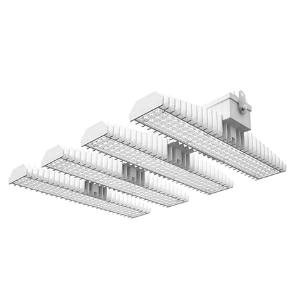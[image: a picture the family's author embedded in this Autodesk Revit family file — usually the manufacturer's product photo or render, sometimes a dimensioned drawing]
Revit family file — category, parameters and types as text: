
# Revit family: 3f_filippi_-_3f_lem_ht_ampio_3f_filippi_-_59028_a0811_-_3f_lem_4_ht_led_120_cr_ampio___vt_8aed
name_source: partatom
category: Lighting Fixtures
units: mm (PartAtom-declared; Revit-internal decimal feet)

## family parameters
Cut with Voids When Loaded = No
Host = Face
Light Source = No
Part Type = Normal
Room Calculation Point = No
Round Connector Dimension = Use Diameter
Shared = No

## types (1)
- 3F Filippi - 3F LEM HT Ampio (1 x LED, 20238 lm, 136 W, 4000 K)
    Apparent Load = 136 VA
    Approval mark = ENEC
    CIE Flux Codes = 60 92 99 100 100
    Color Rendering = 80
    Color Temperature = 4000 K
    Control Gear = Electronic ballast
    Default Elevation = 1800 mm
    Description = Industrial luminaire with high light output and high luminous efficiency designed with the most innovative technologies for environments with temperature up to 70°C.

ILLUMINOTECHNICAL
Luminous efficiency 100% (DLOR 99%, ULOR 1%).
Initial luminous flux of the luminaire 20238 lm.
Direct symmetric wide distribution: the illuminated area has a rectangular shape.
Installation Interdistance Transv.D = 1.58 x hu - Long.D = 1.45 x hu.
Tabular UGR (CIE 117 - 4H-8H; S=0.25H; 70/50/20): RUG 21.3 - 22.4.
Beam angle: 93° - 99°.
Luminous efficacy 149 lm/W.
Lifetime (L93/B10): 30000 h. (tq+25°C)
Lifetime (L90/B10): 50000 h. (tq+25°C)
Lifetime (L85/B10): 80000 h. (tq+25°C)
Lifetime (L80/B10): 100000 h. (tq+25°C)
Lifetime (L85/B10): 50000 h. (tq+70°C)
Sudden decreased luminous flux after 50000 hours: 0% (C0).
Photobiological safety in compliance with IEC/TR 62778: RG0 risk exempt, (IEC 62471).
In compliance with IEC/EN 62722-2-1 - IEC/EN 62717 standards.
Luminous flux at +70°C: -13.5%.

SOURCE
4 Mid-Power linear LED modules 30W/840.
Energy efficiency class (UE 2019/2020 - UE 2019/2015): C.
CIE 13.3 Colour rendering index: CRI >80 (R9 <50%).
IES TM-30 Fidelity Index: Rf = 84 Rg = 95.
CCT nominal colour temperature 4000 K.
Colour initial tolerance (MacAdam): SDCM 3.

MECHANICAL
Passive modular heatsinks in die-casted aluminium, painted in white colour.
To optimize the thermal management of the LED module, the heatsinks are oversized and provided with self-cleaning of cooling fins.
Wiring body in aluminium and galvanised steel anchored solidly to the sinks and thermally separated.
3F Lens lenses with high luminous efficiency, transparent polycarbonate, fixed to the LED modules.
Fixing brackets in stainless steel.
Luminaire with limited surface temperature. - D - (EN 60598-2-24)
Dimensions: 757x542 mm, height 133 mm. Weight 19.273 kg.
IP65 protection degree.
Mechanical strength to impacts IK08 (5 joule).
Glow-wire test resistance 850°C.

ELECTRICAL
Halogen Free electronic wiring 230V-50/60Hz, power factor 0.97, THD <25%, constant output current, class I, 2 driver.
Power of the luminaire 136 W.
CE - IEC 60598-1 - EN 60598-1.
SAFE FLICKER: PstLM=<1 and SVM=<0.4 (IEC TR 61547-1 and IEC TR 63158), to ensure a more comfortable and safe light.
Luminaire compliant with EN 60598-2-22 for power supply from a centralised emergency system CPSS (Central Power Supply System), not incorporated in the luminaire - high risk areas excluded. The default power and flux are 100% in AC and 100% in DC.
Ambient temperature from -30°C to +70°C.
Temperature class T6 max 85°C.
Quick connection via M20 3P connector with 9-13 mm tightening range.
Power unit positioned on a separate compartment by the LED module to ensure optimum temperatures of cabling components, to be inspectable and maintainable.
Relative humidity UR: <85%.

INSTALLATION
Ceiling / Suspended / Wall.
All accessories dedicated to this product are available on the Catalog and on our website www.3F-Filippi.com.

ACCESSORIES
A0811 - VT transparent glass, tempered, not flammable, with sealing gasket.
One required for each light module. The pack contains 10 pieces.

APPLICATIONS
In commercial environments, exhibition and industrial areas, stores, open areas.
Applications with high ambient temperature up to 70°C.

WARNING
Fixture not suitable for cold stores with an ambient temperature <0°C and/or relative humidity >85%.
Luminaire designed for disposal/recycling at end-of-life.
Replaceable (LED only) light source by a professional. Replaceable control gear by a professional.
    Height = 133 mm  [stored 0.436352 ft]
    Lamp = 1 x LED
    Lamp Light Flux = 20238 lm
    Lamp Power = 136 W
    Lamp count = 1
    Length = 757 mm
    Lifetime = 50000 h
    Luminous efficacy = 149 lm/W
    Manufacturer = 3F Filippi
    ModVariant = No
    Model = 3F Filippi - 59028+A0811 - 3F LEM 4 HT LED 120 CR AMPIO + VT
    Mounting Place = Ceiling
    Mounting Type = Pendant
    Number of Poles = 1
    OnlyDefault = Yes
    Power Factor = 1
    Product Name = 3F Filippi - 3F LEM HT Ampio
    Product group = pendant luminaire
    ProductGroupID = 9
    Protection Class = Protection class I
    Protection Degree = IP 65
    RLX_Detail_Level = 1
    RLX_Emergency_Light_Flux = 0 lm
    RLX_Emergency_Type = 0
    RLX_Emergency_Type_DB = No
    RlxData = <blob elided: 117569 chars, md5=81682fd0>
    Socket = socket
    Standby Power = 0 W
    System Light Flux = 20238 lm
    System Power = 136 W
    Type Comments = Product without accessories
    Type Image = 3f_filippi_-_lem_4__a0811.jpg
    URL = http://relux.com
    VarID = ---
    Voltage = 0 V
    Weight = 0.00 kg
    Width = 542 mm

note: [stored X ft] marks values corroborated as IEEE doubles in the binary element streams (Revit-internal decimal feet)

## geometry (parser evidence)
native form markers: Blend x4, Sweep x12
no freeform markers — native parametric forms only
